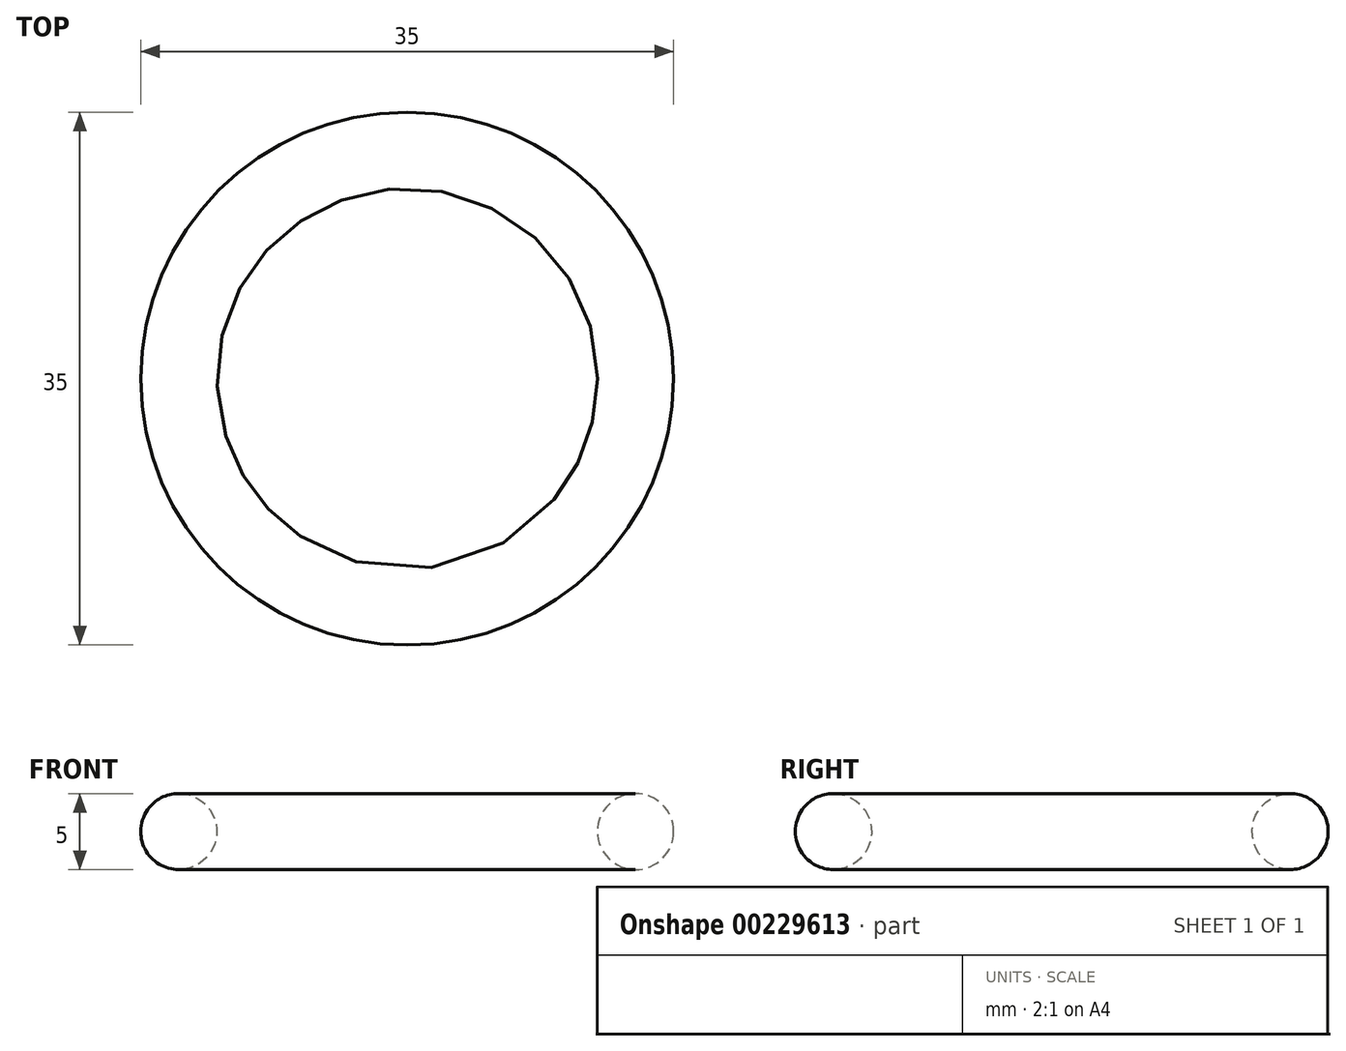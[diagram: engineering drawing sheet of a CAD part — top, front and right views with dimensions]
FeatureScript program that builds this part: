
annotation { "Feature Type Name" : "Feature", "Feature Type Description" : "" }
export const myFeature = defineFeature(function(context is Context, id is Id, definition is map)
    precondition{}
    {
        {
            var Q0;
            Q0=qCreatedBy(makeId("Right.planeOp"),FACE);
            var sketch = newSketch(context, id + "F0", { "sketchPlane" : qUnion([Q0])});
            skLineSegment(sketch, "E0", {"start": v(0, 148.2) * mm, "end": v(0, 0) * mm, "construction": true});
            skSolve(sketch);
        }
        {
            var Q0;
            Q0=qCreatedBy(makeId("Front.planeOp"),FACE);
            var sketch = newSketch(context, id + "F1", { "sketchPlane" : qUnion([Q0])});
            skCircle(sketch, "E1", {"center": v(15, 0) * mm, "radius": 2.5 * mm});
            skSolve(sketch);
        }
        {
            var Q0;
            Q0=makeQuery(id+"F1.imprint","IMPRINT",FACE,{"disambiguationData":[TD([[makeQuery(id+"F1.imprint","IMPRINT",EDGE,{"derivedFrom":sQuery(id+"F1.wireOp",EDGE,"E1")}),1.0]])]});
            var Q1;
            Q1=sQuery(id+"F0.wireOp",EDGE,"E0");
            revolve(context, id + "F2", {"entities" : qUnion([Q0]), "axis" : qUnion([Q1]), "revolveType" : RevolveType.FULL});
        }
    });
